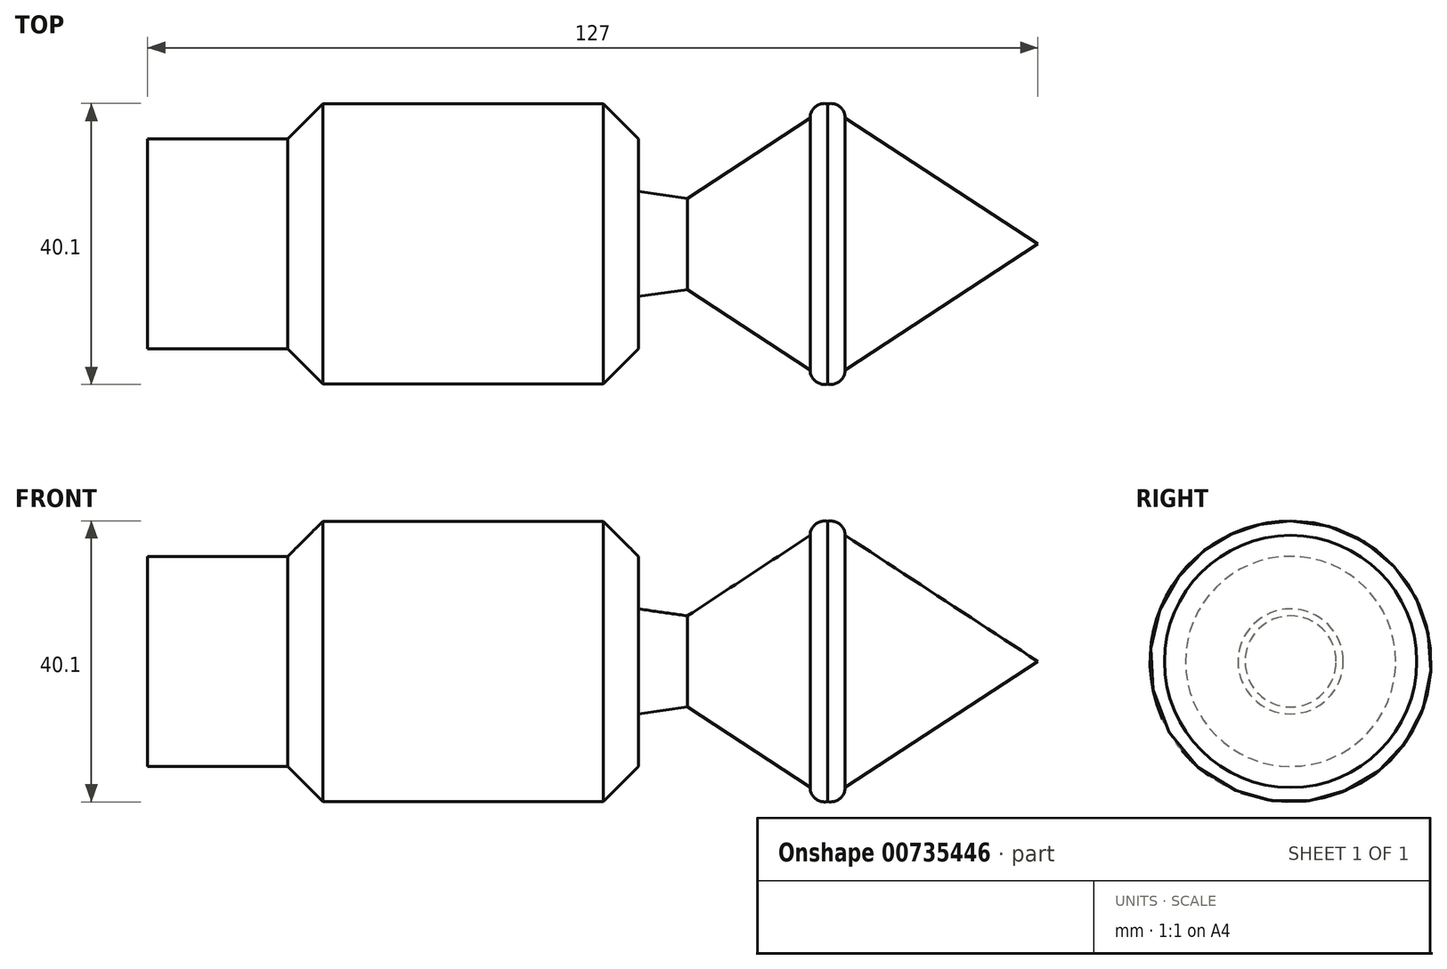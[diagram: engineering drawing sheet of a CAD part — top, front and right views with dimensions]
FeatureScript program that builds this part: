
annotation { "Feature Type Name" : "Feature", "Feature Type Description" : "" }
export const myFeature = defineFeature(function(context is Context, id is Id, definition is map)
    precondition{}
    {
        {
            var Q0;
            Q0=qCreatedBy(makeId("Front.planeOp"),FACE);
            var sketch = newSketch(context, id + "F0", { "sketchPlane" : qUnion([Q0])});
            skLineSegment(sketch, "E0", {"start": v(-52.99, 0) * mm, "end": v(4.01, 0) * mm});
            skLineSegment(sketch, "E1", {"start": v(4.01, 0) * mm, "end": v(44.01, 0) * mm});
            skLineSegment(sketch, "E2", {"start": v(4.01, 0) * mm, "end": v(-2.99, 0) * mm});
            skLineSegment(sketch, "E3", {"start": v(-2.99, 0) * mm, "end": v(-7.99, 0) * mm});
            skLineSegment(sketch, "E4", {"start": v(-47.99, 0) * mm, "end": v(-47.99, 20) * mm});
            skLineSegment(sketch, "E5", {"start": v(-47.99, 20) * mm, "end": v(-7.99, 20) * mm});
            skLineSegment(sketch, "E6", {"start": v(-7.99, 20) * mm, "end": v(-7.99, 0) * mm});
            skLineSegment(sketch, "E7", {"start": v(-2.99, 0) * mm, "end": v(-2.99, 15) * mm});
            skLineSegment(sketch, "E8", {"start": v(-52.99, 0) * mm, "end": v(-52.99, 15) * mm});
            skLineSegment(sketch, "E9", {"start": v(4.01, 0) * mm, "end": v(4.01, 6.5) * mm});
            skLineSegment(sketch, "E10", {"start": v(4.01, 6.5) * mm, "end": v(-2.99, 7.5) * mm});
            skLineSegment(sketch, "E11", {"start": v(24.01, 0) * mm, "end": v(24.01, 20) * mm});
            skLineSegment(sketch, "E12", {"start": v(44.01, 0) * mm, "end": v(54.01, 0) * mm});
            skLineSegment(sketch, "E13", {"start": v(54.01, 0) * mm, "end": v(26.51, 18) * mm});
            skLineSegment(sketch, "E14", {"start": v(21.51, 18) * mm, "end": v(4.01, 6.5) * mm});
            skLineSegment(sketch, "E15", {"start": v(-52.99, 15) * mm, "end": v(-47.99, 20) * mm});
            skLineSegment(sketch, "E16", {"start": v(-7.99, 20) * mm, "end": v(-2.99, 15) * mm});
            skLineSegment(sketch, "E17.MirrorCS", {"start": v(54.01, 0) * mm, "end": v(26.51, -18) * mm});
            skLineSegment(sketch, "E18.MirrorCS", {"start": v(-52.99, -15) * mm, "end": v(-47.99, -20) * mm});
            skLineSegment(sketch, "E19.MirrorCS", {"start": v(4.01, 0) * mm, "end": v(4.01, -6.5) * mm});
            skLineSegment(sketch, "E20.MirrorCS", {"start": v(-7.99, -20) * mm, "end": v(-2.99, -15) * mm});
            skLineSegment(sketch, "E21.MirrorCS", {"start": v(-52.99, 0) * mm, "end": v(-47.99, 0) * mm});
            skLineSegment(sketch, "E22.MirrorCS", {"start": v(4.01, -6.5) * mm, "end": v(-2.99, -7.5) * mm});
            skLineSegment(sketch, "E23.MirrorCS", {"start": v(-2.99, 0) * mm, "end": v(-2.99, -15) * mm});
            skLineSegment(sketch, "E24.MirrorCS", {"start": v(24.01, 0) * mm, "end": v(24.01, -20) * mm});
            skLineSegment(sketch, "E25.MirrorCS", {"start": v(21.51, -18) * mm, "end": v(4.01, -6.5) * mm});
            skLineSegment(sketch, "E26.MirrorCS", {"start": v(-7.99, -20) * mm, "end": v(-7.99, 0) * mm});
            skLineSegment(sketch, "E27.MirrorCS", {"start": v(-52.99, 0) * mm, "end": v(-52.99, -15) * mm});
            skLineSegment(sketch, "E28.MirrorCS", {"start": v(-47.99, -20) * mm, "end": v(-7.99, -20) * mm});
            skLineSegment(sketch, "E29.MirrorCS", {"start": v(-47.99, 0) * mm, "end": v(-47.99, -20) * mm});
            skLineSegment(sketch, "E30", {"start": v(21.51, 18) * mm, "end": v(21.51, 0) * mm});
            skLineSegment(sketch, "E31", {"start": v(21.51, 0) * mm, "end": v(21.51, -18) * mm});
            skLineSegment(sketch, "E32", {"start": v(26.51, -18) * mm, "end": v(26.51, 0) * mm});
            skLineSegment(sketch, "E33", {"start": v(26.51, 0) * mm, "end": v(26.51, 18) * mm});
            skArc(sketch, "E34", {"start": v(21.51, -18) * mm, "mid": v(22.28, -19.6) * mm, "end": v(24.01, -20) * mm});
            skArc(sketch, "E35", {"start": v(24.01, -20) * mm, "mid": v(25.74, -19.6) * mm, "end": v(26.51, -18) * mm});
            skArc(sketch, "E36", {"start": v(24.01, 20) * mm, "mid": v(22.28, 19.6) * mm, "end": v(21.51, 18) * mm});
            skArc(sketch, "E37", {"start": v(26.51, 18) * mm, "mid": v(25.74, 19.6) * mm, "end": v(24.01, 20) * mm});
            skLineSegment(sketch, "E38", {"start": v(-52.99, 15) * mm, "end": v(-72.99, 15) * mm});
            skLineSegment(sketch, "E39", {"start": v(-52.99, -15) * mm, "end": v(-72.99, -15) * mm});
            skLineSegment(sketch, "E40", {"start": v(-72.99, -15) * mm, "end": v(-72.99, 15) * mm});
            skLineSegment(sketch, "E41", {"start": v(-52.99, 0) * mm, "end": v(-72.99, 0) * mm});
            skSolve(sketch);
        }
        {
            var Q0;
            {var subQ0=sQuery(id+"F0.wireOp",EDGE,"E4");Q0=makeQuery(id+"F0.imprint","IMPRINT",FACE,{"disambiguationData":[TD([[makeQuery(id+"F0.imprint","IMPRINT",EDGE,{"derivedFrom":subQ0}),1.0]])]});}
            var Q1;
            {var subQ0=sQuery(id+"F0.wireOp",EDGE,"E4");Q1=makeQuery(id+"F0.imprint","IMPRINT",FACE,{"disambiguationData":[TD([[makeQuery(id+"F0.imprint","IMPRINT",EDGE,{"derivedFrom":subQ0}),-1.0]])]});}
            var Q2;
            {var subQ5=sQuery(id+"F0.wireOp",EDGE,"E6");Q2=makeQuery(id+"F0.imprint","IMPRINT",FACE,{"disambiguationData":[TD([[makeQuery(id+"F0.imprint","IMPRINT",EDGE,{"derivedFrom":subQ5}),1.0]])]});}
            var Q3;
            {var subQ4=sQuery(id+"F0.wireOp",EDGE,"E9");Q3=makeQuery(id+"F0.imprint","IMPRINT",FACE,{"disambiguationData":[TD([[makeQuery(id+"F0.imprint","IMPRINT",EDGE,{"derivedFrom":subQ4}),1.0]])]});}
            var Q4;
            {var subQ0=sQuery(id+"F0.wireOp",EDGE,"E9");Q4=makeQuery(id+"F0.imprint","IMPRINT",FACE,{"disambiguationData":[TD([[makeQuery(id+"F0.imprint","IMPRINT",EDGE,{"derivedFrom":subQ0}),-1.0]])]});}
            var Q5;
            {var subQ0=sQuery(id+"F0.wireOp",EDGE,"E11");Q5=makeQuery(id+"F0.imprint","IMPRINT",FACE,{"disambiguationData":[TD([[makeQuery(id+"F0.imprint","IMPRINT",EDGE,{"derivedFrom":subQ0}),1.0]])]});}
            var Q6;
            {var subQ0=sQuery(id+"F0.wireOp",EDGE,"E11");Q6=makeQuery(id+"F0.imprint","IMPRINT",FACE,{"disambiguationData":[TD([[makeQuery(id+"F0.imprint","IMPRINT",EDGE,{"derivedFrom":subQ0}),-1.0]])]});}
            var Q7;
            Q7=makeQuery(id+"F0.imprint","IMPRINT",FACE,{"disambiguationData":[TD([[makeQuery(id+"F0.imprint","IMPRINT",EDGE,{"derivedFrom":sQuery(id+"F0.wireOp",EDGE,"E13")}),1.0]])]});
            var Q8;
            Q8=makeQuery(id+"F0.imprint","IMPRINT",FACE,{"disambiguationData":[TD([[makeQuery(id+"F0.imprint","IMPRINT",EDGE,{"derivedFrom":sQuery(id+"F0.wireOp",EDGE,"E8")}),1.0]])]});
            var Q9;
            Q9=sQuery(id+"F0.wireOp",EDGE,"E0");
            revolve(context, id + "F1", {"surfaceOperationType" : NewSurfaceOperationType.NEW, "entities" : qUnion([Q0, Q1, Q2, Q3, Q4, Q5, Q6, Q7, Q8]), "axis" : qUnion([Q9]), "revolveType" : RevolveType.FULL});
        }
    });
